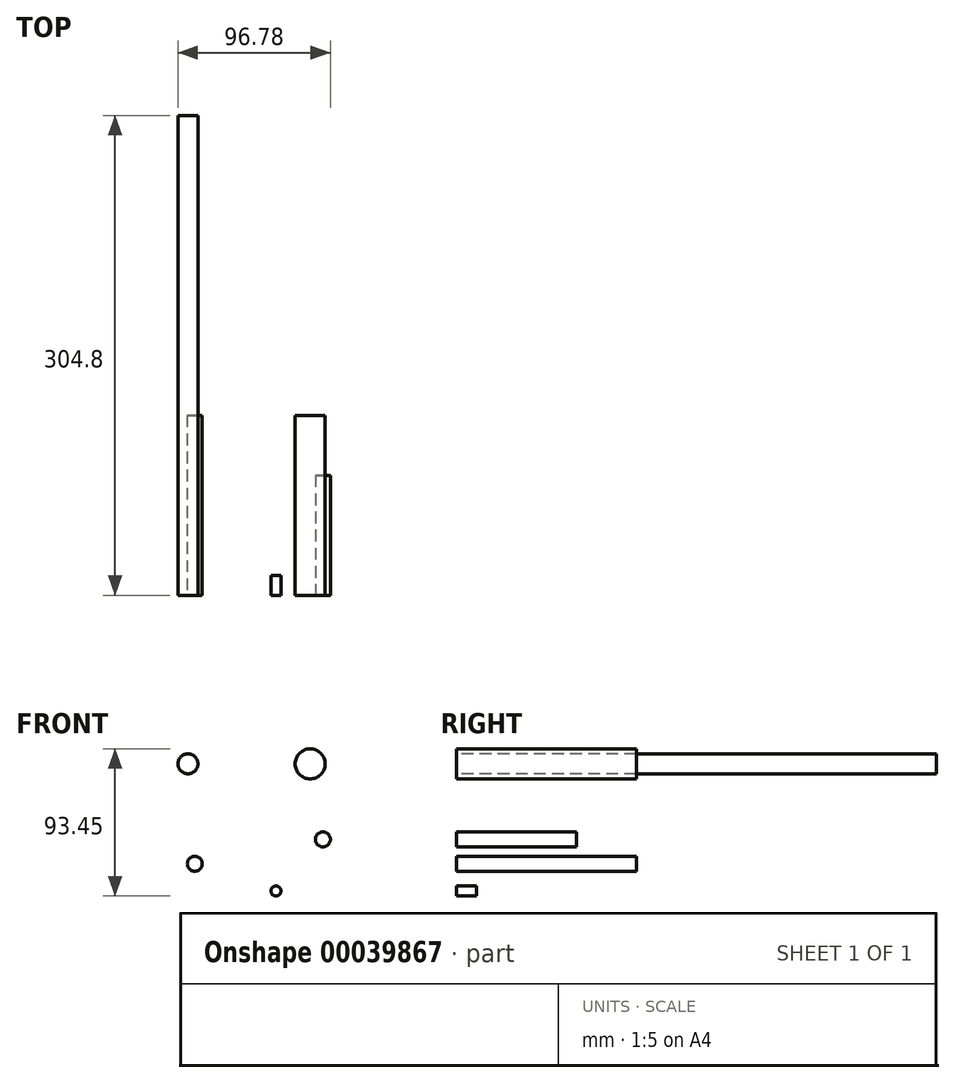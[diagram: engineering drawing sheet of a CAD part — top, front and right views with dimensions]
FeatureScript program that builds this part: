
annotation { "Feature Type Name" : "Feature", "Feature Type Description" : "" }
export const myFeature = defineFeature(function(context is Context, id is Id, definition is map)
    precondition{}
    {
        {
            var Q0;
            Q0=qCreatedBy(makeId("Front.planeOp"),FACE);
            var sketch = newSketch(context, id + "F0", { "sketchPlane" : qUnion([Q0])});
            skCircle(sketch, "E0", {"center": v(-48.27, 53.49) * mm, "radius": 6.35 * mm});
            skSolve(sketch);
        }
        {
            var Q0;
            Q0 = qSketchRegion(id + "F0", true);
            extrude(context, id + "F1", {"entities" : qUnion([Q0]), "oppositeDirection" : true, "depth" : 304.8 * mm});
        }
        {
            var Q0;
            Q0=qCreatedBy(makeId("Front.planeOp"),FACE);
            var sketch = newSketch(context, id + "F2", { "sketchPlane" : qUnion([Q0])});
            skCircle(sketch, "E1", {"center": v(29.35, 53.49) * mm, "radius": 9.53 * mm});
            skSolve(sketch);
        }
        {
            var Q0;
            Q0=makeQuery(id+"F2.imprint","IMPRINT",FACE,{"disambiguationData":[TD([[makeQuery(id+"F2.imprint","IMPRINT",EDGE,{"derivedFrom":sQuery(id+"F2.wireOp",EDGE,"E1")}),1.0]])]});
            extrude(context, id + "F3", {"entities" : qUnion([Q0]), "oppositeDirection" : true, "depth" : 114.3 * mm});
        }
        {
            var Q0;
            Q0=qCreatedBy(makeId("Front.planeOp"),FACE);
            var sketch = newSketch(context, id + "F4", { "sketchPlane" : qUnion([Q0])});
            skCircle(sketch, "E2", {"center": v(-43.95, -9.98) * mm, "radius": 4.76 * mm});
            skSolve(sketch);
        }
        {
            var Q0;
            Q0 = qSketchRegion(id + "F4", true);
            extrude(context, id + "F5", {"entities" : qUnion([Q0]), "oppositeDirection" : true, "depth" : 114.3 * mm});
        }
        {
            var Q0;
            Q0=qCreatedBy(makeId("Front.planeOp"),FACE);
            var sketch = newSketch(context, id + "F6", { "sketchPlane" : qUnion([Q0])});
            skCircle(sketch, "E3", {"center": v(37.4, 5.51) * mm, "radius": 4.76 * mm});
            skSolve(sketch);
        }
        {
            var Q0;
            Q0 = qSketchRegion(id + "F6", true);
            extrude(context, id + "F7", {"entities" : qUnion([Q0]), "oppositeDirection" : true, "depth" : 76.2 * mm});
        }
        {
            var Q0;
            Q0=qCreatedBy(makeId("Front.planeOp"),FACE);
            var sketch = newSketch(context, id + "F8", { "sketchPlane" : qUnion([Q0])});
            skCircle(sketch, "E4", {"center": v(7.6, -27.27) * mm, "radius": 3.18 * mm});
            skSolve(sketch);
        }
        {
            var Q0;
            Q0 = qSketchRegion(id + "F8", true);
            extrude(context, id + "F9", {"entities" : qUnion([Q0]), "oppositeDirection" : true, "depth" : 12.7 * mm});
        }
    });
